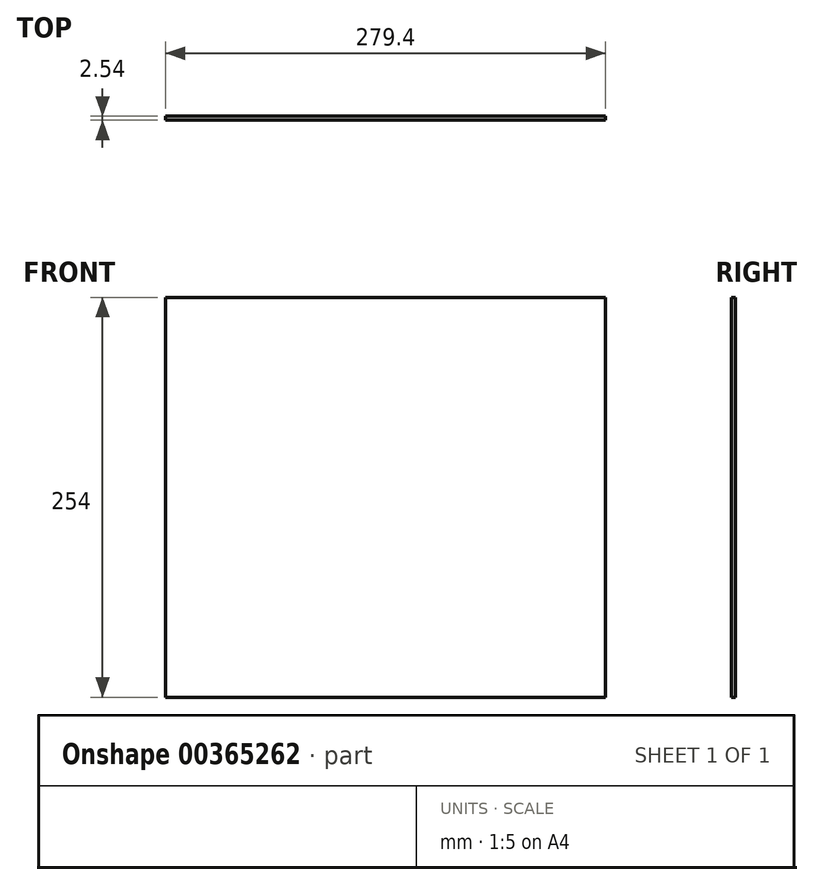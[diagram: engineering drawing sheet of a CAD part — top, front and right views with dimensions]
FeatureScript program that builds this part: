
annotation { "Feature Type Name" : "Feature", "Feature Type Description" : "" }
export const myFeature = defineFeature(function(context is Context, id is Id, definition is map)
    precondition{}
    {
        {
            var Q0;
            Q0=qCreatedBy(makeId("Front.planeOp"),FACE);
            var sketch = newSketch(context, id + "F0", { "sketchPlane" : qUnion([Q0])});
            skLineSegment(sketch, "E0.bottom", {"start": v(-163.42, 145.7) * mm, "end": v(115.98, 145.7) * mm});
            skLineSegment(sketch, "E0.top", {"start": v(-163.42, -108.3) * mm, "end": v(115.98, -108.3) * mm});
            skLineSegment(sketch, "E0.left", {"start": v(-163.42, 145.7) * mm, "end": v(-163.42, -108.3) * mm});
            skLineSegment(sketch, "E0.right", {"start": v(115.98, 145.7) * mm, "end": v(115.98, -108.3) * mm});
            skSolve(sketch);
        }
        {
            var Q0;
            Q0=qSketchRegion(id+"F0",true);
            extrude(context, id + "F1", {"entities" : qUnion([Q0]), "depth" : 2.54 * mm});
        }
    });
